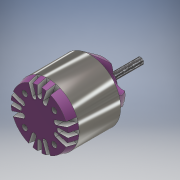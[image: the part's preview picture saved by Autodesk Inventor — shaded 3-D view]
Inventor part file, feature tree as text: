
AUTODESK INVENTOR PART (.ipt)
format: ipt  version: 2017 (Build 210142000, 142)  size: 329,216 bytes
history: native  units: mm
features: sketch x4, pattern_circular x3, extrude x2, other x1, revolve x1, hole x1
ambient origin geometry x8: Origin, YZ Plane, XZ Plane, XY Plane, X Axis, Y Axis, Z Axis, Center Point
bodies: Body1 (feature_tree)
feature tree (12):
  other  "Bryła1"
  revolve  "Obrót1"
  extrude  "Wyciągnięcie proste2"  Depth=14.0mm
  pattern_circular  "Szyk kołowy1"  [2 undecoded]
  hole  "Otwór1"  [1 undecoded]
  pattern_circular  "Szyk kołowy2"  [2 undecoded]
  extrude  "Wyciągnięcie proste3"  Depth=19.0mm
  pattern_circular  "Szyk kołowy3"  Count=2  [1 undecoded]
  sketch  "Szkic1"
  sketch  "Szkic2"
  sketch  "Szkic3"
  sketch  "Szkic4"
note: 6 required parameter values undecoded (feature->parameter linkage not recoverable at this tier; creation-order binding heuristic only, values carry confidence <= 0.55)
